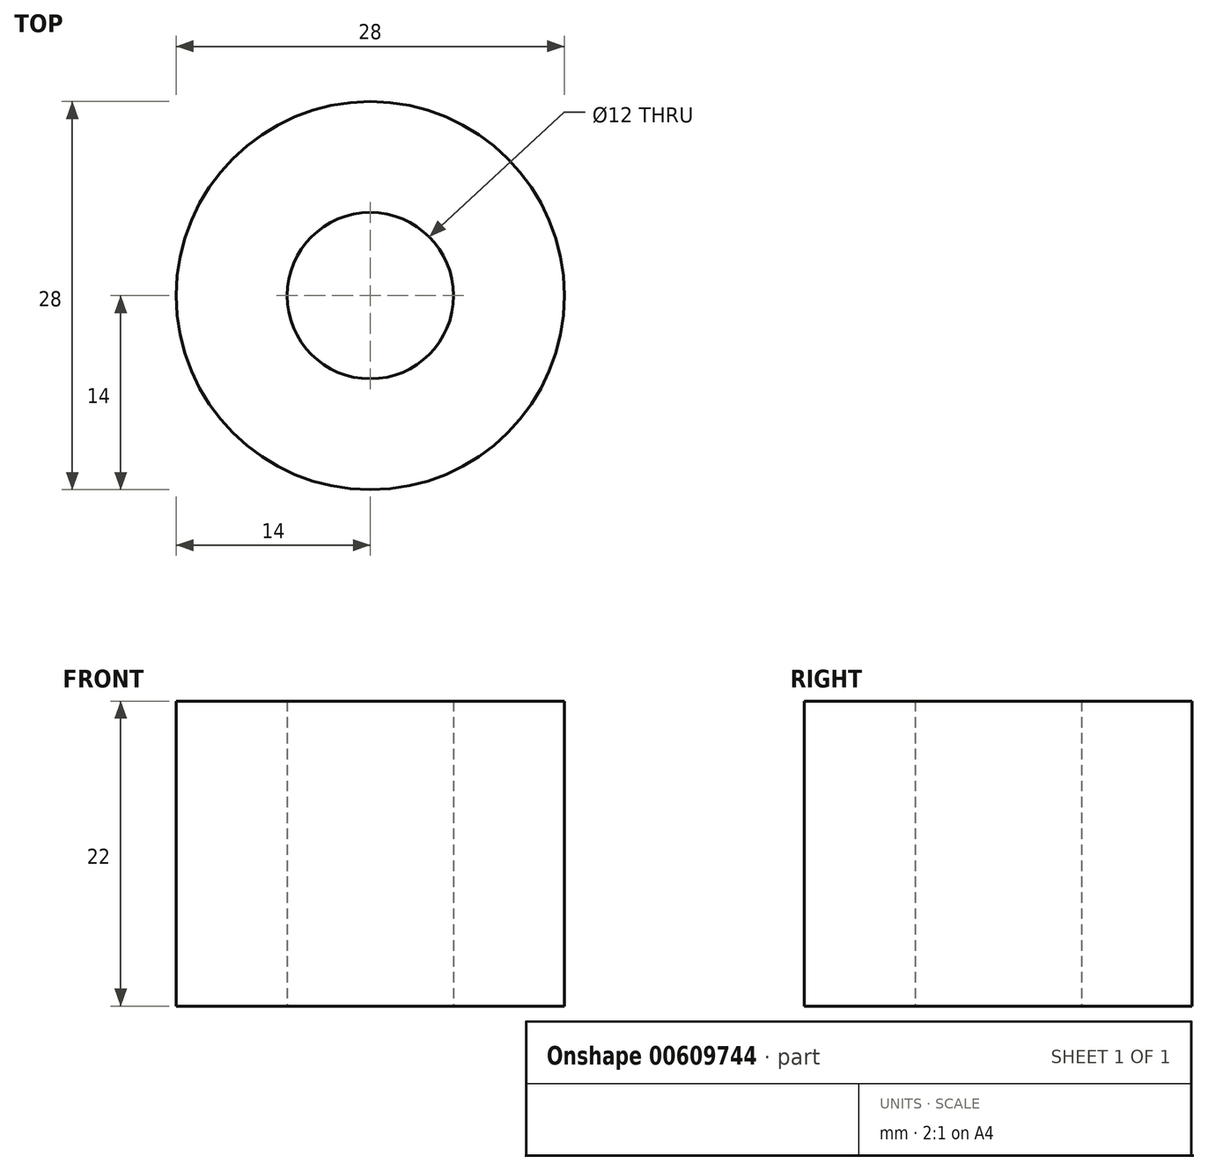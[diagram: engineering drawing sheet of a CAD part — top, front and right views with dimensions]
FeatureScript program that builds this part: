
annotation { "Feature Type Name" : "Feature", "Feature Type Description" : "" }
export const myFeature = defineFeature(function(context is Context, id is Id, definition is map)
    precondition{}
    {
        {
            var Q0;
            Q0=qCreatedBy(makeId("Top.planeOp"),FACE);
            var sketch = newSketch(context, id + "F0", { "sketchPlane" : qUnion([Q0])});
            skCircle(sketch, "E0", {"center": v(0, 0) * mm, "radius": 14 * mm});
            skCircle(sketch, "E1", {"center": v(0, 0) * mm, "radius": 6 * mm});
            skSolve(sketch);
        }
        {
            var Q0;
            Q0 = qSketchRegion(id + "F0", true);
            extrude(context, id + "F1", {"entities" : qUnion([Q0]), "depth" : 22 * mm, "offsetDistance" : 25 * mm});
        }
    });
